# Revit family: EKF_EE_ПанельПНЩРМ_PROxima
name_source: partatom
category: Электрооборудование
units: mm (PartAtom-declared; Revit-internal decimal feet)

## family parameters
Всегда вертикально = Нет
На основе рабочей плоскости = Да
Общий = Да
При загрузке вырезать с полостями = Нет
Размер круглого соединителя = Использовать диаметр
Тип детали = Силовой щит
Точка расчета площади = Нет

## types (2) — shared parameters
ADSK_Единица измерения = шт.
ADSK_Завод-изготовитель = EKF
ADSK_Количество = 1
ADSK_Марка = Панель ПН
ADSK_Материал = Сталь_Оцинкованная
ADSK_Обозначение = Панель ПН
ADSK_Размер_Высота = 140 мм
ADSK_Размер_Глубина = 1.5 мм
D = 7 мм
T = 1.5 мм
Высота = 154 мм
Загиб1 = Да
Загиб1_Ширина = 29 мм
Загиб2_Ширина = 10 мм
Изготовитель = EKF
Отв_Кол = 2
Отступ = 16 мм
Серия номенклатуры = PROxima
Степень защиты IP = -
ТВ = EKF_2
Тип установки = -
Шаг = 76 мм
zero-valued in all types: ADSK_Масса, Отметка по умолчанию

## per-type parameters (varying)
| type | ADSK_Код изделия | ADSK_Наименование | ADSK_Размер_Ширина | ОтвН_Кол | Отступ2 | Отступ_ОтвН | Тип |
| Панель ПН 140x545мм (ЩРНМ-8, ЩРНМ-9) | ppn-140x545 | Панель ПН 140x545мм (ЩРНМ-8 ЩРНМ-9) | 545 мм | 6 | 11 мм | 66 мм | 138 мм |
| Панель ПН 140x745мм (ЩРНМ-8L, ЩРНМ-9L) | ppn-140x745 | Панель ПН 140x745мм (ЩРНМ-8L ЩРНМ-9L) | 745 мм | 9 | 9 мм | 75 мм | 139 мм |
